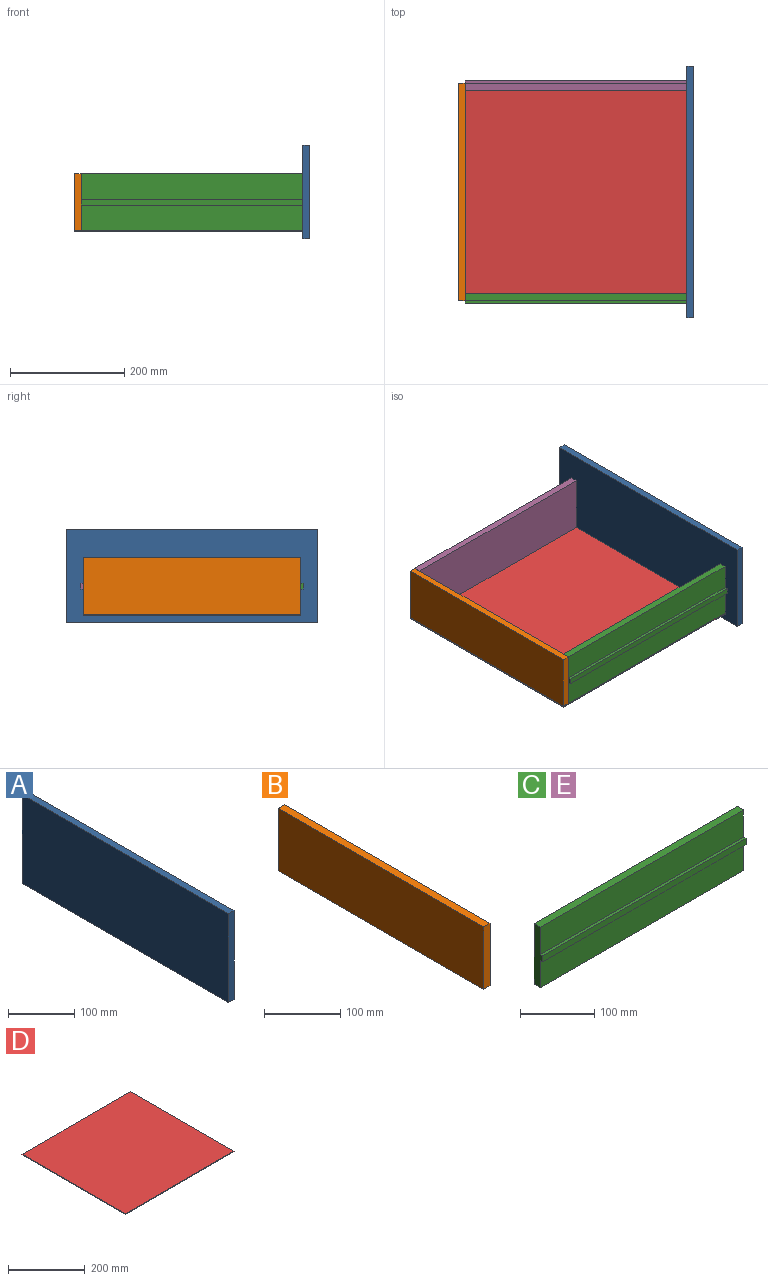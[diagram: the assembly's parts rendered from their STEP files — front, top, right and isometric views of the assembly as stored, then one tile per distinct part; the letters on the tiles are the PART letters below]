
ASSEMBLY  parts=5 mates=4
PART A: 6 faces, bbox 12x440x164 mm
  f0: plane 440x12mm, normal (0,0,1), area 5280mm2, adj f1,f3,f4,f5
  f1: plane 164x12mm, normal (0,-1,0), area 1968mm2, adj f0,f2,f4,f5
  f2: plane 440x12mm, normal (0,0,-1), area 5280mm2, adj f1,f3,f4,f5
  f3: plane 164x12mm, normal (0,1,0), area 1968mm2, adj f0,f2,f4,f5
  f4: plane 440x164mm, normal (1,0,0), area 72160mm2, adj f0,f1,f2,f3
  f5: plane 440x164mm, normal (-1,0,0), area 72160mm2, adj f0,f1,f2,f3
PART B: 6 faces, bbox 12x380x100 mm
  f0: plane 100x12mm, normal (0,1,0), area 1200mm2, adj f1,f3,f4,f5
  f1: plane 380x12mm, normal (0,0,1), area 4560mm2, adj f0,f2,f4,f5
  f2: plane 100x12mm, normal (0,-1,0), area 1200mm2, adj f1,f3,f4,f5
  f3: plane 380x12mm, normal (0,0,-1), area 4560mm2, adj f0,f2,f4,f5
  f4: plane 380x100mm, normal (1,0,0), area 38000mm2, adj f0,f1,f2,f3
  f5: plane 380x100mm, normal (-1,0,0), area 38000mm2, adj f0,f1,f2,f3
PART C: 10 faces, bbox 388x17x100 mm
  f0: plane 388x45mm, normal (0,-1,0), area 17460mm2, adj f1,f2,f3,f7
  f1: plane 100x17mm, normal (1,0,0), area 1250mm2, adj f0,f2,f4,f5,f6,f7,f8,f9
  f2: plane 388x12mm, normal (0,0,1), area 4656mm2, adj f0,f1,f3,f6
  f3: plane 100x17mm, normal (-1,0,0), area 1250mm2, adj f0,f2,f4,f5,f6,f7,f8,f9
  f4: plane 388x12mm, normal (0,0,-1), area 4656mm2, adj f1,f3,f5,f6
  f5: plane 388x45mm, normal (0,-1,0), area 17460mm2, adj f1,f3,f4,f8
  f6: plane 388x100mm, normal (0,1,0), area 38800mm2, adj f1,f2,f3,f4
  f7: plane 388x5mm, normal (0,0,1), area 1940mm2, adj f0,f1,f3,f9
  f8: plane 388x5mm, normal (0,0,-1), area 1940mm2, adj f1,f3,f5,f9
  f9: plane 388x10mm, normal (0,-1,0), area 3880mm2, adj f1,f3,f7,f8
PART D: 6 faces, bbox 400x380x2 mm
  f0: plane 400x2mm, normal (0,1,0), area 800mm2, adj f1,f3,f4,f5
  f1: plane 380x2mm, normal (-1,0,0), area 760mm2, adj f0,f2,f4,f5
  f2: plane 400x2mm, normal (0,-1,0), area 800mm2, adj f1,f3,f4,f5
  f3: plane 380x2mm, normal (1,0,0), area 760mm2, adj f0,f2,f4,f5
  f4: plane 400x380mm, normal (0,0,1), area 152000mm2, adj f0,f1,f2,f3
  f5: plane 400x380mm, normal (0,0,-1), area 152000mm2, adj f0,f1,f2,f3
PART E: same geometry as C
PLACE A t=(-12,0,0)mm
PLACE B t=(-406,0,-18)mm
PLACE C t=(-206,-184,-18)mm
PLACE D t=(-212,0,-70)mm
PLACE E rot(axis=(0,0,-1),180deg) t=(-206,184,-18)mm
MATE fastened C.f1 <-> A.f5  axis (1,0,0) through (-12,-190,-68)mm
MATE fastened D.f4 <-> B.f3  axis (0,0,1) through (-412,190,-68)mm
MATE fastened E.f1 <-> B.f4  axis (-1,0,0) through (-400,190,32)mm
MATE fastened B.f4 <-> C.f3  axis (1,0,0) through (-400,-190,-68)mm
